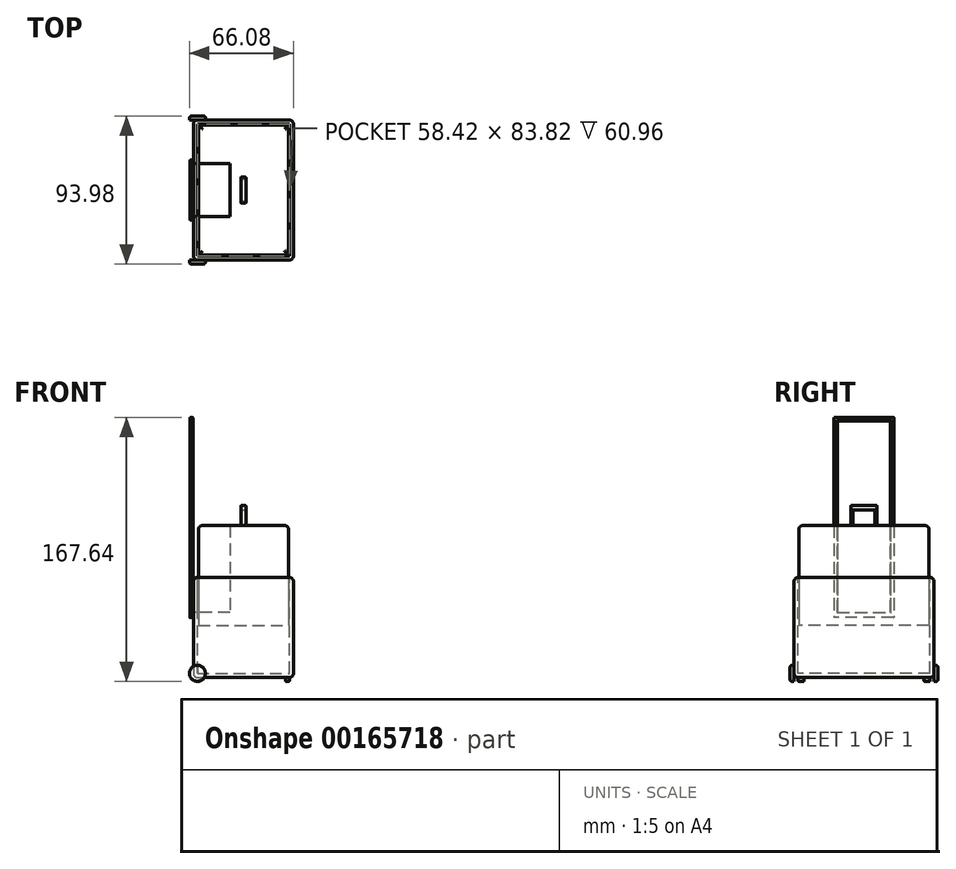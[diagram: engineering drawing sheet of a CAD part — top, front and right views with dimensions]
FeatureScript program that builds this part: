
annotation { "Feature Type Name" : "Feature", "Feature Type Description" : "" }
export const myFeature = defineFeature(function(context is Context, id is Id, definition is map)
    precondition{}
    {
        {
            var Q0;
            Q0=qCreatedBy(makeId("Top.planeOp"),FACE);
            var sketch = newSketch(context, id + "F0", { "sketchPlane" : qUnion([Q0])});
            skLineSegment(sketch, "E0.bottom", {"start": v(-36.13, 40.32) * mm, "end": v(27.37, 40.32) * mm});
            skLineSegment(sketch, "E0.top", {"start": v(-36.13, -48.58) * mm, "end": v(27.37, -48.58) * mm});
            skLineSegment(sketch, "E0.left", {"start": v(-36.13, 40.32) * mm, "end": v(-36.13, -48.58) * mm});
            skLineSegment(sketch, "E0.right", {"start": v(27.37, 40.32) * mm, "end": v(27.37, -48.58) * mm});
            skSolve(sketch);
        }
        {
            var Q0;
            Q0=qSketchRegion(id+"F0",true);
            extrude(context, id + "F1", {"entities" : qUnion([Q0]), "depth" : 63.5 * mm});
        }
        {
            var Q0;
            Q0=makeQuery(id+"F1.opExtrude","SWEPT_EDGE",EDGE,{"disambiguationData":[OSD([sQuery(id+"F0.wireOp",EDGE,"E0.top"),sQuery(id+"F0.wireOp",EDGE,"E0.left")])]});
            var Q1;
            Q1=makeQuery(id+"F1.opExtrude","SWEPT_EDGE",EDGE,{"disambiguationData":[OSD([sQuery(id+"F0.wireOp",EDGE,"E0.top"),sQuery(id+"F0.wireOp",EDGE,"E0.right")])]});
            var Q2;
            Q2=makeQuery(id+"F1.opExtrude","SWEPT_EDGE",EDGE,{"disambiguationData":[OSD([sQuery(id+"F0.wireOp",EDGE,"E0.bottom"),sQuery(id+"F0.wireOp",EDGE,"E0.right")])]});
            var Q3;
            Q3=makeQuery(id+"F1.opExtrude","CAP_EDGE",EDGE,{"disambiguationData":[OSD([sQuery(id+"F0.wireOp",EDGE,"E0.right")])],"isStart":true});
            var Q4;
            Q4=makeQuery(id+"F1.opExtrude","CAP_EDGE",EDGE,{"disambiguationData":[OSD([sQuery(id+"F0.wireOp",EDGE,"E0.top")])],"isStart":true});
            var Q5;
            Q5=makeQuery(id+"F1.opExtrude","CAP_EDGE",EDGE,{"disambiguationData":[OSD([sQuery(id+"F0.wireOp",EDGE,"E0.bottom")])],"isStart":true});
            var Q6;
            Q6=makeQuery(id+"F1.opExtrude","CAP_EDGE",EDGE,{"disambiguationData":[OSD([sQuery(id+"F0.wireOp",EDGE,"E0.left")])],"isStart":true});
            var Q7;
            Q7=makeQuery(id+"F1.opExtrude","SWEPT_EDGE",EDGE,{"disambiguationData":[OSD([sQuery(id+"F0.wireOp",EDGE,"E0.bottom"),sQuery(id+"F0.wireOp",EDGE,"E0.left")])]});
            fillet(context, id + "F2", {"entities" : qUnion([Q0, Q1, Q2, Q3, Q4, Q5, Q6, Q7]), "radius" : 2.54 * mm, "tangentPropagation" : true, "allowEdgeOverflow" : false});
        }
        {
            var Q0;
            Q0=makeQuery(id+"F1.opExtrude","CAP_FACE",FACE,{"disambiguationData":[OSD([sQuery(id+"F0.wireOp",EDGE,"E0.bottom"),sQuery(id+"F0.wireOp",EDGE,"E0.top"),sQuery(id+"F0.wireOp",EDGE,"E0.left"),sQuery(id+"F0.wireOp",EDGE,"E0.right")])],"isStart":false});
            shell(context, id + "F3", {"entities" : qUnion([Q0]), "thickness" : 2.54 * mm});
        }
        {
            var Q0;
            Q0=makeQuery(id+"F3.opShell","OFFSET_FACE",FACE,{"disambiguationData":[OSD([sQuery(id+"F0.wireOp",EDGE,"E0.bottom"),sQuery(id+"F0.wireOp",EDGE,"E0.top"),sQuery(id+"F0.wireOp",EDGE,"E0.left"),sQuery(id+"F0.wireOp",EDGE,"E0.right")])]});
            cPlane(context, id + "F4", {"entities" : qUnion([Q0]), "cplaneType" : CPlaneType.OFFSET, "offset" : 30.48 * mm, "width" : 152.4 * mm, "height" : 152.4 * mm});
        }
        {
            var Q0;
            Q0=qCreatedBy(id+"F4.planeOp",FACE);
            var sketch = newSketch(context, id + "F5", { "sketchPlane" : qUnion([Q0])});
            skLineSegment(sketch, "E1.bottom", {"start": v(-32.98, 37.11) * mm, "end": v(24.21, 37.11) * mm});
            skLineSegment(sketch, "E1.top", {"start": v(-32.98, -45.53) * mm, "end": v(24.21, -45.53) * mm});
            skLineSegment(sketch, "E1.left", {"start": v(-32.98, 37.11) * mm, "end": v(-32.98, -45.53) * mm});
            skLineSegment(sketch, "E1.right", {"start": v(24.21, 37.11) * mm, "end": v(24.21, -45.53) * mm});
            skSolve(sketch);
        }
        {
            var Q0;
            Q0=makeQuery(id+"F5.imprint","IMPRINT",FACE,{"disambiguationData":[TD([[makeQuery(id+"F5.imprint","IMPRINT",EDGE,{"derivedFrom":sQuery(id+"F5.wireOp",EDGE,"E1.bottom")}),-1.0]])]});
            extrude(context, id + "F6", {"entities" : qUnion([Q0]), "depth" : 63.5 * mm});
        }
        {
            var Q0;
            Q0=makeQuery(id+"F1.opExtrude","CAP_FACE",FACE,{"disambiguationData":[OSD([sQuery(id+"F0.wireOp",EDGE,"E0.bottom"),sQuery(id+"F0.wireOp",EDGE,"E0.top"),sQuery(id+"F0.wireOp",EDGE,"E0.left"),sQuery(id+"F0.wireOp",EDGE,"E0.right")])],"isStart":true});
            cPlane(context, id + "F7", {"entities" : qUnion([Q0]), "cplaneType" : CPlaneType.OFFSET, "offset" : 38.1 * mm, "oppositeDirection" : true, "width" : 152.4 * mm, "height" : 152.4 * mm});
        }
        {
            var Q0;
            Q0=qCreatedBy(id+"F7.planeOp",FACE);
            var sketch = newSketch(context, id + "F8", { "sketchPlane" : qUnion([Q0])});
            skLineSegment(sketch, "E2.bottom", {"start": v(-36.35, -14.92) * mm, "end": v(-38.36, -14.92) * mm});
            skLineSegment(sketch, "E2.top", {"start": v(-36.35, 23.18) * mm, "end": v(-38.36, 23.18) * mm});
            skLineSegment(sketch, "E2.left", {"start": v(-36.35, -14.92) * mm, "end": v(-36.35, 23.18) * mm});
            skLineSegment(sketch, "E2.right", {"start": v(-38.36, -14.92) * mm, "end": v(-38.36, 23.18) * mm});
            skSolve(sketch);
        }
        {
            var Q0;
            Q0=qSketchRegion(id+"F8",true);
            extrude(context, id + "F9", {"entities" : qUnion([Q0]), "oppositeDirection" : true, "depth" : 127 * mm});
        }
        {
            var Q0;
            Q0=makeQuery(id+"F9.opExtrude","SWEPT_FACE",FACE,{"disambiguationData":[OSD([sQuery(id+"F8.wireOp",EDGE,"E2.right")])]});
            var sketch = newSketch(context, id + "F10", { "sketchPlane" : qUnion([Q0])});
            skLineSegment(sketch, "E3.bottom", {"start": v(-12.71, 162.99) * mm, "end": v(20.93, 162.99) * mm});
            skLineSegment(sketch, "E3.top", {"start": v(-12.71, 41.45) * mm, "end": v(20.93, 41.45) * mm});
            skLineSegment(sketch, "E3.left", {"start": v(-12.71, 162.99) * mm, "end": v(-12.71, 41.45) * mm});
            skLineSegment(sketch, "E3.right", {"start": v(20.93, 162.99) * mm, "end": v(20.93, 41.45) * mm});
            skSolve(sketch);
        }
        {
            var Q0;
            Q0=makeQuery(id+"F10.imprint","IMPRINT",FACE,{"disambiguationData":[TD([[makeQuery(id+"F10.imprint","IMPRINT",EDGE,{"derivedFrom":sQuery(id+"F10.wireOp",EDGE,"E3.bottom")}),-1.0]])]});
            extrude(context, id + "F11", {"entities" : qUnion([Q0]), "operationType" : NewBodyOperationType.REMOVE, "oppositeDirection" : true, "depth" : 25.4 * mm});
        }
        {
            var Q0;
            Q0=makeQuery(id+"F6.opExtrude","CAP_EDGE",EDGE,{"disambiguationData":[OSD([sQuery(id+"F5.wireOp",EDGE,"E1.right")])],"isStart":false});
            var Q1;
            Q1=makeQuery(id+"F6.opExtrude","CAP_EDGE",EDGE,{"disambiguationData":[OSD([sQuery(id+"F5.wireOp",EDGE,"E1.top")])],"isStart":false});
            var Q2;
            Q2=makeQuery(id+"F6.opExtrude","CAP_EDGE",EDGE,{"disambiguationData":[OSD([sQuery(id+"F5.wireOp",EDGE,"E1.left")])],"isStart":false});
            var Q3;
            Q3=makeQuery(id+"F6.opExtrude","CAP_EDGE",EDGE,{"disambiguationData":[OSD([sQuery(id+"F5.wireOp",EDGE,"E1.bottom")])],"isStart":false});
            fillet(context, id + "F12", {"entities" : qUnion([Q0, Q1, Q2, Q3]), "radius" : 2.54 * mm, "tangentPropagation" : true, "allowEdgeOverflow" : false});
        }
        {
            var Q0;
            Q0=makeQuery(id+"F1.opExtrude","SWEPT_FACE",FACE,{"disambiguationData":[OSD([sQuery(id+"F0.wireOp",EDGE,"E0.top")])]});
            cPlane(context, id + "F13", {"entities" : qUnion([Q0]), "cplaneType" : CPlaneType.OFFSET, "offset" : 2.54 * mm, "width" : 152.4 * mm, "height" : 152.4 * mm});
        }
        {
            var Q0;
            Q0=qCreatedBy(id+"F13.planeOp",FACE);
            var sketch = newSketch(context, id + "F14", { "sketchPlane" : qUnion([Q0])});
            skCircle(sketch, "E4", {"center": v(-33.63, 2.63) * mm, "radius": 5.08 * mm});
            skSolve(sketch);
        }
        {
            var Q0;
            Q0=makeQuery(id+"F14.imprint","IMPRINT",FACE,{"disambiguationData":[TD([[makeQuery(id+"F14.imprint","IMPRINT",EDGE,{"derivedFrom":sQuery(id+"F14.wireOp",EDGE,"E4")}),1.0]])]});
            extrude(context, id + "F15", {"entities" : qUnion([Q0]), "operationType" : NewBodyOperationType.ADD, "oppositeDirection" : true, "depth" : 2.54 * mm});
        }
        {
            var Q0;
            Q0=makeQuery(id+"F1.opExtrude","SWEPT_FACE",FACE,{"disambiguationData":[OSD([sQuery(id+"F0.wireOp",EDGE,"E0.bottom")])]});
            cPlane(context, id + "F16", {"entities" : qUnion([Q0]), "cplaneType" : CPlaneType.OFFSET, "offset" : 2.54 * mm, "width" : 152.4 * mm, "height" : 152.4 * mm});
        }
        {
            var Q0;
            Q0=qCreatedBy(id+"F16.planeOp",FACE);
            var sketch = newSketch(context, id + "F17", { "sketchPlane" : qUnion([Q0])});
            skCircle(sketch, "E5", {"center": v(33.54, 2.55) * mm, "radius": 5.08 * mm});
            skSolve(sketch);
        }
        {
            var Q0;
            Q0=qSketchRegion(id+"F17",true);
            extrude(context, id + "F18", {"entities" : qUnion([Q0]), "oppositeDirection" : true, "depth" : 2.54 * mm});
        }
        {
            var Q0;
            Q0=makeQuery(id+"F15.opExtrude","CAP_EDGE",EDGE,{"disambiguationData":[OSD([sQuery(id+"F14.wireOp",EDGE,"E4")])],"isStart":true});
            fillet(context, id + "F19", {"entities" : qUnion([Q0]), "radius" : 1.27 * mm, "tangentPropagation" : true, "allowEdgeOverflow" : false});
        }
        {
            var Q0;
            Q0=makeQuery(id+"F18.opExtrude","CAP_EDGE",EDGE,{"disambiguationData":[OSD([sQuery(id+"F17.wireOp",EDGE,"E5")])],"isStart":true});
            fillet(context, id + "F20", {"entities" : qUnion([Q0]), "radius" : 1.27 * mm, "tangentPropagation" : true, "allowEdgeOverflow" : false});
        }
        {
            var Q0;
            Q0=makeQuery(id+"F1.opExtrude","CAP_FACE",FACE,{"disambiguationData":[OSD([sQuery(id+"F0.wireOp",EDGE,"E0.bottom"),sQuery(id+"F0.wireOp",EDGE,"E0.top"),sQuery(id+"F0.wireOp",EDGE,"E0.left"),sQuery(id+"F0.wireOp",EDGE,"E0.right")])],"isStart":true});
            var sketch = newSketch(context, id + "F21", { "sketchPlane" : qUnion([Q0])});
            skLineSegment(sketch, "E6.bottom", {"start": v(24.83, 46.04) * mm, "end": v(22.29, 46.04) * mm});
            skLineSegment(sketch, "E6.top", {"start": v(24.83, 42.23) * mm, "end": v(22.29, 42.23) * mm});
            skLineSegment(sketch, "E6.left", {"start": v(24.83, 46.04) * mm, "end": v(24.83, 42.23) * mm});
            skLineSegment(sketch, "E6.right", {"start": v(22.29, 46.04) * mm, "end": v(22.29, 42.23) * mm});
            skSolve(sketch);
        }
        {
            var Q0;
            Q0=makeQuery(id+"F21.imprint","IMPRINT",FACE,{"disambiguationData":[TD([[makeQuery(id+"F21.imprint","IMPRINT",EDGE,{"derivedFrom":sQuery(id+"F21.wireOp",EDGE,"E6.bottom")}),1.0]])]});
            extrude(context, id + "F22", {"entities" : qUnion([Q0]), "operationType" : NewBodyOperationType.ADD, "depth" : 2.54 * mm});
        }
        {
            var Q0;
            Q0=makeQuery(id+"F22.opExtrude","CAP_EDGE",EDGE,{"disambiguationData":[OSD([sQuery(id+"F21.wireOp",EDGE,"E6.top")])],"isStart":false});
            var Q1;
            Q1=makeQuery(id+"F22.opExtrude","CAP_EDGE",EDGE,{"disambiguationData":[OSD([sQuery(id+"F21.wireOp",EDGE,"E6.right")])],"isStart":false});
            var Q2;
            Q2=makeQuery(id+"F22.opExtrude","CAP_EDGE",EDGE,{"disambiguationData":[OSD([sQuery(id+"F21.wireOp",EDGE,"E6.bottom")])],"isStart":false});
            var Q3;
            Q3=makeQuery(id+"F22.opExtrude","CAP_EDGE",EDGE,{"disambiguationData":[OSD([sQuery(id+"F21.wireOp",EDGE,"E6.left")])],"isStart":false});
            var Q4;
            Q4=makeQuery(id+"F22.opExtrude","SWEPT_EDGE",EDGE,{"disambiguationData":[OSD([sQuery(id+"F0.wireOp",EDGE,"E0.bottom"),sQuery(id+"F0.wireOp",EDGE,"E0.top"),sQuery(id+"F0.wireOp",EDGE,"E0.left"),sQuery(id+"F0.wireOp",EDGE,"E0.right"),sQuery(id+"F21.wireOp",EDGE,"E6.top"),sQuery(id+"F21.wireOp",EDGE,"E6.left")])]});
            var Q5;
            Q5=makeQuery(id+"F22.opExtrude","SWEPT_EDGE",EDGE,{"disambiguationData":[OSD([sQuery(id+"F21.wireOp",EDGE,"E6.top"),sQuery(id+"F21.wireOp",EDGE,"E6.right")])]});
            var Q6;
            Q6=makeQuery(id+"F22.opExtrude","SWEPT_EDGE",EDGE,{"disambiguationData":[OSD([sQuery(id+"F0.wireOp",EDGE,"E0.bottom"),sQuery(id+"F0.wireOp",EDGE,"E0.top"),sQuery(id+"F0.wireOp",EDGE,"E0.left"),sQuery(id+"F0.wireOp",EDGE,"E0.right"),sQuery(id+"F21.wireOp",EDGE,"E6.bottom"),sQuery(id+"F21.wireOp",EDGE,"E6.right")])]});
            var Q7;
            Q7=makeQuery(id+"F22.opExtrude","SWEPT_EDGE",EDGE,{"disambiguationData":[OSD([sQuery(id+"F21.wireOp",EDGE,"E6.bottom"),sQuery(id+"F21.wireOp",EDGE,"E6.left")])]});
            fillet(context, id + "F23", {"entities" : qUnion([Q0, Q1, Q2, Q3, Q4, Q5, Q6, Q7]), "radius" : 0.5 * mm, "tangentPropagation" : true, "allowEdgeOverflow" : false});
        }
        {
            var Q0;
            Q0=makeQuery(id+"F1.opExtrude","CAP_FACE",FACE,{"disambiguationData":[OSD([sQuery(id+"F0.wireOp",EDGE,"E0.bottom"),sQuery(id+"F0.wireOp",EDGE,"E0.top"),sQuery(id+"F0.wireOp",EDGE,"E0.left"),sQuery(id+"F0.wireOp",EDGE,"E0.right")])],"isStart":true});
            var sketch = newSketch(context, id + "F24", { "sketchPlane" : qUnion([Q0])});
            skLineSegment(sketch, "E7.bottom", {"start": v(24.83, -37.78) * mm, "end": v(22.29, -37.78) * mm});
            skLineSegment(sketch, "E7.top", {"start": v(24.83, -33.97) * mm, "end": v(22.29, -33.97) * mm});
            skLineSegment(sketch, "E7.left", {"start": v(24.83, -37.78) * mm, "end": v(24.83, -33.97) * mm});
            skLineSegment(sketch, "E7.right", {"start": v(22.29, -37.78) * mm, "end": v(22.29, -33.97) * mm});
            skSolve(sketch);
        }
        {
            var Q0;
            Q0=qSketchRegion(id+"F24",true);
            extrude(context, id + "F25", {"entities" : qUnion([Q0]), "operationType" : NewBodyOperationType.ADD, "depth" : 2.54 * mm});
        }
        {
            var Q0;
            Q0=makeQuery(id+"F25.opExtrude","SWEPT_EDGE",EDGE,{"disambiguationData":[OSD([sQuery(id+"F24.wireOp",EDGE,"E7.bottom"),sQuery(id+"F24.wireOp",EDGE,"E7.left")])]});
            var Q1;
            Q1=makeQuery(id+"F25.opExtrude","SWEPT_EDGE",EDGE,{"disambiguationData":[OSD([sQuery(id+"F0.wireOp",EDGE,"E0.bottom"),sQuery(id+"F0.wireOp",EDGE,"E0.top"),sQuery(id+"F0.wireOp",EDGE,"E0.left"),sQuery(id+"F0.wireOp",EDGE,"E0.right"),sQuery(id+"F24.wireOp",EDGE,"E7.bottom"),sQuery(id+"F24.wireOp",EDGE,"E7.right")])]});
            var Q2;
            Q2=makeQuery(id+"F25.opExtrude","CAP_EDGE",EDGE,{"disambiguationData":[OSD([sQuery(id+"F24.wireOp",EDGE,"E7.bottom")])],"isStart":false});
            var Q3;
            Q3=makeQuery(id+"F25.opExtrude","CAP_EDGE",EDGE,{"disambiguationData":[OSD([sQuery(id+"F24.wireOp",EDGE,"E7.right")])],"isStart":false});
            var Q4;
            Q4=makeQuery(id+"F25.opExtrude","CAP_EDGE",EDGE,{"disambiguationData":[OSD([sQuery(id+"F24.wireOp",EDGE,"E7.top")])],"isStart":false});
            var Q5;
            Q5=makeQuery(id+"F25.opExtrude","CAP_EDGE",EDGE,{"disambiguationData":[OSD([sQuery(id+"F24.wireOp",EDGE,"E7.left")])],"isStart":false});
            var Q6;
            Q6=makeQuery(id+"F25.opExtrude","SWEPT_EDGE",EDGE,{"disambiguationData":[OSD([sQuery(id+"F0.wireOp",EDGE,"E0.bottom"),sQuery(id+"F0.wireOp",EDGE,"E0.top"),sQuery(id+"F0.wireOp",EDGE,"E0.left"),sQuery(id+"F0.wireOp",EDGE,"E0.right"),sQuery(id+"F24.wireOp",EDGE,"E7.top"),sQuery(id+"F24.wireOp",EDGE,"E7.left")])]});
            var Q7;
            Q7=makeQuery(id+"F25.opExtrude","SWEPT_EDGE",EDGE,{"disambiguationData":[OSD([sQuery(id+"F24.wireOp",EDGE,"E7.top"),sQuery(id+"F24.wireOp",EDGE,"E7.right")])]});
            fillet(context, id + "F26", {"entities" : qUnion([Q0, Q1, Q2, Q3, Q4, Q5, Q6, Q7]), "radius" : 0.5 * mm, "tangentPropagation" : true, "allowEdgeOverflow" : false});
        }
        {
            var Q0;
            Q0=makeQuery(id+"F6.opExtrude","CAP_FACE",FACE,{"disambiguationData":[OSD([sQuery(id+"F5.wireOp",EDGE,"E1.bottom"),sQuery(id+"F5.wireOp",EDGE,"E1.top"),sQuery(id+"F5.wireOp",EDGE,"E1.left"),sQuery(id+"F5.wireOp",EDGE,"E1.right")])],"isStart":false});
            var sketch = newSketch(context, id + "F27", { "sketchPlane" : qUnion([Q0])});
            skLineSegment(sketch, "E8.bottom", {"start": v(-6.03, 4.1) * mm, "end": v(-2.84, 4.1) * mm});
            skLineSegment(sketch, "E8.top", {"start": v(-6.03, -12.5) * mm, "end": v(-2.84, -12.5) * mm});
            skLineSegment(sketch, "E8.left", {"start": v(-6.03, 4.1) * mm, "end": v(-6.03, -12.5) * mm});
            skLineSegment(sketch, "E8.right", {"start": v(-2.84, 4.1) * mm, "end": v(-2.84, -12.5) * mm});
            skSolve(sketch);
        }
        {
            var Q0;
            Q0=makeQuery(id+"F27.imprint","IMPRINT",FACE,{"disambiguationData":[TD([[makeQuery(id+"F27.imprint","IMPRINT",EDGE,{"derivedFrom":sQuery(id+"F27.wireOp",EDGE,"E8.bottom")}),-1.0]])]});
            extrude(context, id + "F28", {"entities" : qUnion([Q0]), "operationType" : NewBodyOperationType.ADD, "depth" : 12.7 * mm});
        }
        {
            var Q0;
            Q0=makeQuery(id+"F28.opExtrude","SWEPT_FACE",FACE,{"disambiguationData":[OSD([sQuery(id+"F27.wireOp",EDGE,"E8.right")])]});
            var sketch = newSketch(context, id + "F29", { "sketchPlane" : qUnion([Q0])});
            skLineSegment(sketch, "E9.bottom", {"start": v(-11.23, 106.5) * mm, "end": v(2.8, 106.5) * mm});
            skLineSegment(sketch, "E9.top", {"start": v(-11.23, 96.52) * mm, "end": v(2.8, 96.52) * mm});
            skLineSegment(sketch, "E9.left", {"start": v(-11.23, 106.5) * mm, "end": v(-11.23, 96.52) * mm});
            skLineSegment(sketch, "E9.right", {"start": v(2.8, 106.5) * mm, "end": v(2.8, 96.52) * mm});
            skSolve(sketch);
        }
        {
            var Q0;
            Q0=qSketchRegion(id+"F29",true);
            extrude(context, id + "F30", {"entities" : qUnion([Q0]), "operationType" : NewBodyOperationType.REMOVE, "oppositeDirection" : true, "depth" : 25.4 * mm});
        }
        {
            var Q0;
            Q0=makeQuery(id+"F9.opExtrude","SWEPT_EDGE",EDGE,{"disambiguationData":[OSD([sQuery(id+"F8.wireOp",EDGE,"E2.top"),sQuery(id+"F8.wireOp",EDGE,"E2.left")])]});
            var Q1;
            Q1=makeQuery(id+"F9.opExtrude","CAP_EDGE",EDGE,{"disambiguationData":[OSD([sQuery(id+"F8.wireOp",EDGE,"E2.left")])],"isStart":false});
            var Q2;
            Q2=makeQuery(id+"F9.opExtrude","SWEPT_EDGE",EDGE,{"disambiguationData":[OSD([sQuery(id+"F8.wireOp",EDGE,"E2.bottom"),sQuery(id+"F8.wireOp",EDGE,"E2.left")])]});
            var Q3;
            Q3=makeQuery(id+"F11.boolean.opBoolean","INTERSECT",EDGE,{"derivedFrom":[makeQuery(id+"F9.opExtrude","SWEPT_FACE",FACE,{"disambiguationData":[OSD([sQuery(id+"F8.wireOp",EDGE,"E2.left")])]}),makeQuery(id+"F11.opExtrude","SWEPT_FACE",FACE,{"disambiguationData":[OSD([sQuery(id+"F10.wireOp",EDGE,"E3.left")])]})]});
            var Q4;
            Q4=makeQuery(id+"F11.boolean.opBoolean","INTERSECT",EDGE,{"derivedFrom":[makeQuery(id+"F9.opExtrude","SWEPT_FACE",FACE,{"disambiguationData":[OSD([sQuery(id+"F8.wireOp",EDGE,"E2.left")])]}),makeQuery(id+"F11.opExtrude","SWEPT_FACE",FACE,{"disambiguationData":[OSD([sQuery(id+"F10.wireOp",EDGE,"E3.right")])]})]});
            var Q5;
            Q5=makeQuery(id+"F11.boolean.opBoolean","INTERSECT",EDGE,{"derivedFrom":[makeQuery(id+"F9.opExtrude","SWEPT_FACE",FACE,{"disambiguationData":[OSD([sQuery(id+"F8.wireOp",EDGE,"E2.left")])]}),makeQuery(id+"F11.opExtrude","SWEPT_FACE",FACE,{"disambiguationData":[OSD([sQuery(id+"F10.wireOp",EDGE,"E3.bottom")])]})]});
            fillet(context, id + "F31", {"entities" : qUnion([Q0, Q1, Q2, Q3, Q4, Q5]), "radius" : 0.5 * mm, "tangentPropagation" : true, "allowEdgeOverflow" : false});
        }
        {
            var Q0;
            Q0=makeQuery(id+"F9.opExtrude","CAP_EDGE",EDGE,{"disambiguationData":[OSD([sQuery(id+"F8.wireOp",EDGE,"E2.right")])],"isStart":false});
            var Q1;
            Q1=makeQuery(id+"F11.boolean.opBoolean","COPY",EDGE,{"derivedFrom":makeQuery(id+"F11.opExtrude","CAP_EDGE",EDGE,{"disambiguationData":[OSD([sQuery(id+"F10.wireOp",EDGE,"E3.bottom")])],"isStart":true})});
            var Q2;
            Q2=makeQuery(id+"F11.boolean.opBoolean","COPY",EDGE,{"derivedFrom":makeQuery(id+"F11.opExtrude","CAP_EDGE",EDGE,{"disambiguationData":[OSD([sQuery(id+"F10.wireOp",EDGE,"E3.left")])],"isStart":true})});
            var Q3;
            Q3=makeQuery(id+"F11.boolean.opBoolean","COPY",EDGE,{"derivedFrom":makeQuery(id+"F11.opExtrude","CAP_EDGE",EDGE,{"disambiguationData":[OSD([sQuery(id+"F10.wireOp",EDGE,"E3.right")])],"isStart":true})});
            var Q4;
            Q4=makeQuery(id+"F9.opExtrude","SWEPT_EDGE",EDGE,{"disambiguationData":[OSD([sQuery(id+"F8.wireOp",EDGE,"E2.top"),sQuery(id+"F8.wireOp",EDGE,"E2.right")])]});
            var Q5;
            Q5=makeQuery(id+"F9.opExtrude","SWEPT_EDGE",EDGE,{"disambiguationData":[OSD([sQuery(id+"F8.wireOp",EDGE,"E2.bottom"),sQuery(id+"F8.wireOp",EDGE,"E2.right")])]});
            fillet(context, id + "F32", {"entities" : qUnion([Q0, Q1, Q2, Q3, Q4, Q5]), "radius" : 0.5 * mm, "tangentPropagation" : true, "allowEdgeOverflow" : false});
        }
        {
            var Q0;
            Q0=makeQuery(id+"F1.opExtrude","CAP_EDGE",EDGE,{"disambiguationData":[OSD([sQuery(id+"F0.wireOp",EDGE,"E0.right")])],"isStart":false});
            var Q1;
            Q1=makeQuery(id+"F1.opExtrude","CAP_EDGE",EDGE,{"disambiguationData":[OSD([sQuery(id+"F0.wireOp",EDGE,"E0.top")])],"isStart":false});
            var Q2;
            Q2=makeQuery(id+"F1.opExtrude","CAP_EDGE",EDGE,{"disambiguationData":[OSD([sQuery(id+"F0.wireOp",EDGE,"E0.bottom")])],"isStart":false});
            var Q3;
            Q3=makeQuery(id+"F1.opExtrude","CAP_EDGE",EDGE,{"disambiguationData":[OSD([sQuery(id+"F0.wireOp",EDGE,"E0.left")])],"isStart":false});
            fillet(context, id + "F33", {"entities" : qUnion([Q0, Q1, Q2, Q3]), "radius" : 2.54 * mm, "tangentPropagation" : true, "allowEdgeOverflow" : false});
        }
        {
            var Q0;
            Q0=makeQuery(id+"F28.opExtrude","CAP_EDGE",EDGE,{"disambiguationData":[OSD([sQuery(id+"F27.wireOp",EDGE,"E8.right")])],"isStart":false});
            var Q1;
            Q1=makeQuery(id+"F30.boolean.opBoolean","COPY",EDGE,{"derivedFrom":makeQuery(id+"F30.opExtrude","CAP_EDGE",EDGE,{"disambiguationData":[OSD([sQuery(id+"F29.wireOp",EDGE,"E9.bottom")])],"isStart":true})});
            var Q2;
            Q2=makeQuery(id+"F30.boolean.opBoolean","COPY",EDGE,{"derivedFrom":makeQuery(id+"F30.opExtrude","CAP_EDGE",EDGE,{"disambiguationData":[OSD([sQuery(id+"F29.wireOp",EDGE,"E9.left")])],"isStart":true})});
            var Q3;
            Q3=makeQuery(id+"F28.opExtrude","SWEPT_EDGE",EDGE,{"disambiguationData":[OSD([sQuery(id+"F27.wireOp",EDGE,"E8.top"),sQuery(id+"F27.wireOp",EDGE,"E8.right")])]});
            var Q4;
            Q4=makeQuery(id+"F30.boolean.opBoolean","COPY",EDGE,{"derivedFrom":makeQuery(id+"F30.opExtrude","CAP_EDGE",EDGE,{"disambiguationData":[OSD([sQuery(id+"F29.wireOp",EDGE,"E9.right")])],"isStart":true})});
            var Q5;
            Q5=makeQuery(id+"F28.opExtrude","SWEPT_EDGE",EDGE,{"disambiguationData":[OSD([sQuery(id+"F27.wireOp",EDGE,"E8.bottom"),sQuery(id+"F27.wireOp",EDGE,"E8.right")])]});
            var Q6;
            Q6=makeQuery(id+"F28.opExtrude","CAP_EDGE",EDGE,{"disambiguationData":[OSD([sQuery(id+"F27.wireOp",EDGE,"E8.top")])],"isStart":false});
            var Q7;
            Q7=makeQuery(id+"F28.opExtrude","CAP_EDGE",EDGE,{"disambiguationData":[OSD([sQuery(id+"F27.wireOp",EDGE,"E8.bottom")])],"isStart":false});
            var Q8;
            Q8=makeQuery(id+"F28.opExtrude","CAP_EDGE",EDGE,{"disambiguationData":[OSD([sQuery(id+"F27.wireOp",EDGE,"E8.left")])],"isStart":false});
            var Q9;
            Q9=makeQuery(id+"F28.opExtrude","SWEPT_EDGE",EDGE,{"disambiguationData":[OSD([sQuery(id+"F27.wireOp",EDGE,"E8.top"),sQuery(id+"F27.wireOp",EDGE,"E8.left")])]});
            var Q10;
            Q10=makeQuery(id+"F28.opExtrude","SWEPT_EDGE",EDGE,{"disambiguationData":[OSD([sQuery(id+"F27.wireOp",EDGE,"E8.bottom"),sQuery(id+"F27.wireOp",EDGE,"E8.left")])]});
            var Q11;
            Q11=makeQuery(id+"F30.boolean.opBoolean","INTERSECT",EDGE,{"derivedFrom":[makeQuery(id+"F28.opExtrude","SWEPT_FACE",FACE,{"disambiguationData":[OSD([sQuery(id+"F27.wireOp",EDGE,"E8.left")])]}),makeQuery(id+"F30.opExtrude","SWEPT_FACE",FACE,{"disambiguationData":[OSD([sQuery(id+"F29.wireOp",EDGE,"E9.bottom")])]})]});
            fillet(context, id + "F34", {"entities" : qUnion([Q0, Q1, Q2, Q3, Q4, Q5, Q6, Q7, Q8, Q9, Q10, Q11]), "radius" : 0.5 * mm, "tangentPropagation" : true, "allowEdgeOverflow" : false});
        }
    });
